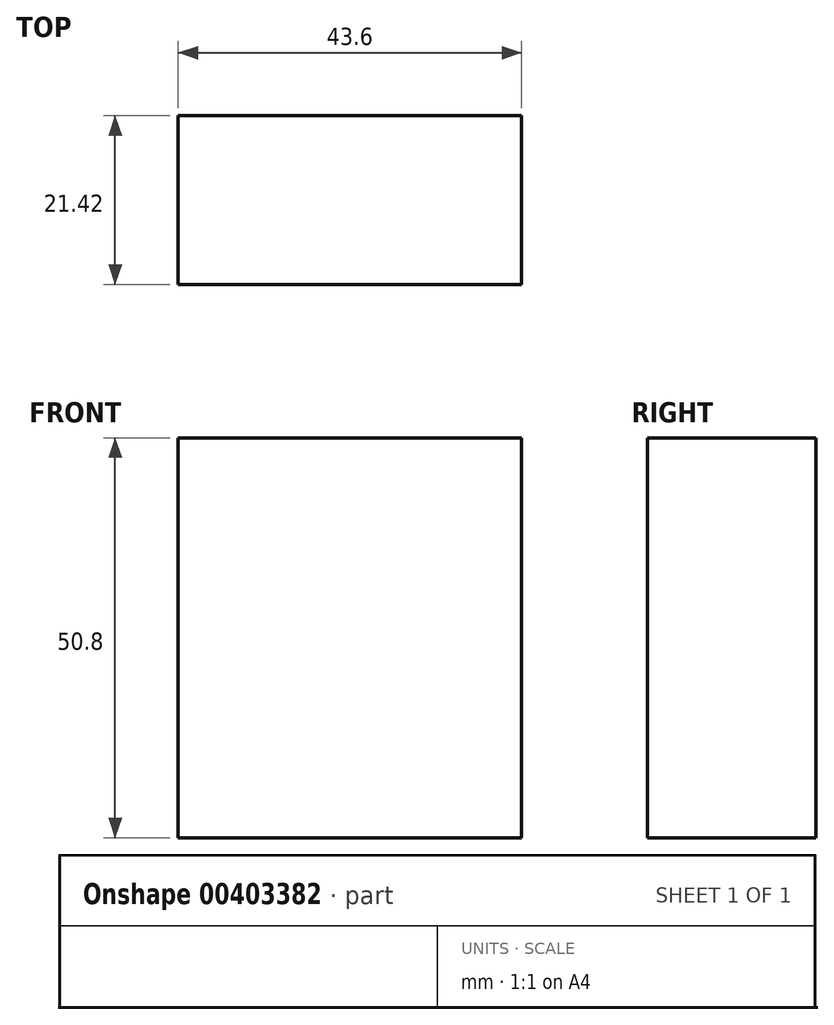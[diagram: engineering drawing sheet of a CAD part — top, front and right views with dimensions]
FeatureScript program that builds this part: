
annotation { "Feature Type Name" : "Feature", "Feature Type Description" : "" }
export const myFeature = defineFeature(function(context is Context, id is Id, definition is map)
    precondition{}
    {
        {
            var Q0;
            Q0=qCreatedBy(makeId("Top.planeOp"),FACE);
            var sketch = newSketch(context, id + "F0", { "sketchPlane" : qUnion([Q0])});
            skLineSegment(sketch, "E0.bottom", {"start": v(21.8, -10.7) * mm, "end": v(-21.8, -10.7) * mm});
            skLineSegment(sketch, "E0.top", {"start": v(21.8, 10.7) * mm, "end": v(-21.8, 10.7) * mm});
            skLineSegment(sketch, "E0.left", {"start": v(21.8, -10.7) * mm, "end": v(21.8, 10.7) * mm});
            skLineSegment(sketch, "E0.right", {"start": v(-21.8, -10.7) * mm, "end": v(-21.8, 10.7) * mm});
            skPoint(sketch, "E0.middle", {"position": v(0, 0) * mm});
            skSolve(sketch);
        }
        {
            var Q0;
            Q0=makeQuery(id+"F0.imprint","IMPRINT",FACE,{"disambiguationData":[TD([[makeQuery(id+"F0.imprint","IMPRINT",EDGE,{"derivedFrom":sQuery(id+"F0.wireOp",EDGE,"E0.bottom")}),-1.0]])]});
            extrude(context, id + "F1", {"entities" : qUnion([Q0]), "depth" : 50.8 * mm});
        }
    });
